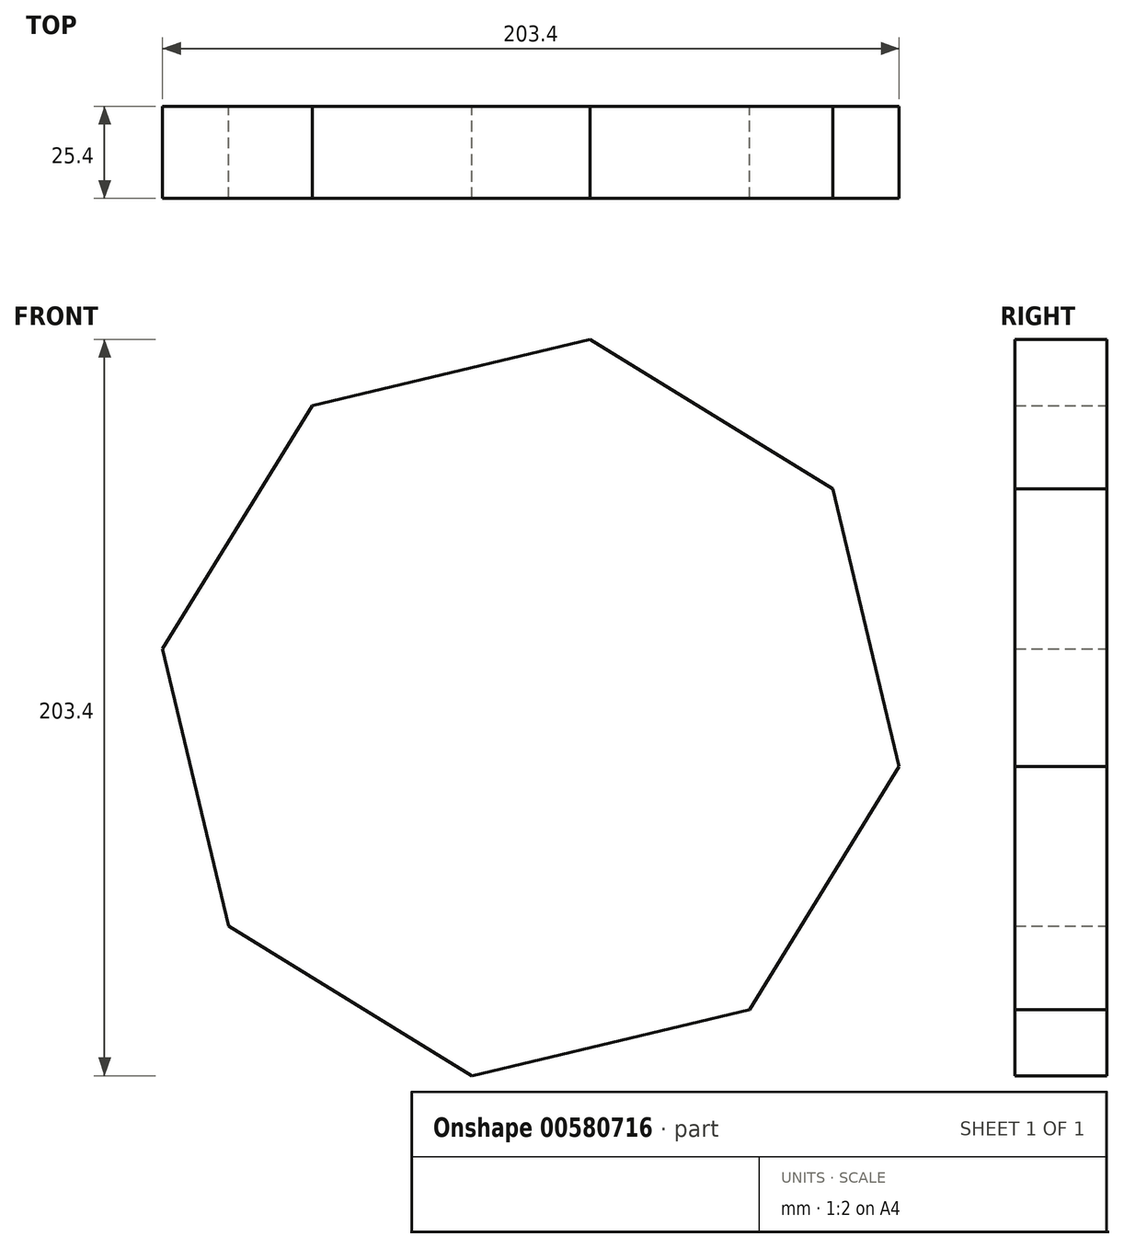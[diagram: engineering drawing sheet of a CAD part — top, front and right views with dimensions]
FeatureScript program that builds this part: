
annotation { "Feature Type Name" : "Feature", "Feature Type Description" : "" }
export const myFeature = defineFeature(function(context is Context, id is Id, definition is map)
    precondition{}
    {
        {
            var Q0;
            Q0=qCreatedBy(makeId("Front.planeOp"),FACE);
            var sketch = newSketch(context, id + "F0", { "sketchPlane" : qUnion([Q0])});
            skCircle(sketch, "E0.cCircle", {"center": v(0, 0) * mm, "radius": 91.98 * mm, "construction": true});
            skLineSegment(sketch, "E0.0", {"start": v(-98.3, 15.75) * mm, "end": v(-58.38, 80.65) * mm});
            skLineSegment(sketch, "E0.1", {"start": v(-58.38, 80.65) * mm, "end": v(15.75, 98.3) * mm, "construction": true});
            skLineSegment(sketch, "E0.2", {"start": v(15.75, 98.3) * mm, "end": v(80.65, 58.38) * mm});
            skLineSegment(sketch, "E0.3", {"start": v(80.65, 58.38) * mm, "end": v(98.3, -15.75) * mm});
            skLineSegment(sketch, "E0.4", {"start": v(98.3, -15.75) * mm, "end": v(58.38, -80.65) * mm});
            skLineSegment(sketch, "E0.5", {"start": v(58.38, -80.65) * mm, "end": v(-15.75, -98.3) * mm});
            skLineSegment(sketch, "E0.6", {"start": v(-15.75, -98.3) * mm, "end": v(-80.65, -58.38) * mm});
            skLineSegment(sketch, "E0.7", {"start": v(-80.65, -58.38) * mm, "end": v(-98.3, 15.75) * mm});
            skPoint(sketch, "E0.0.midPoint", {"position": v(-78.34, 48.2) * mm});
            skLineSegment(sketch, "E1.0", {"start": v(-101.7, 16.3) * mm, "end": v(-60.4, 83.43) * mm});
            skLineSegment(sketch, "E1.1", {"start": v(-83.43, -60.4) * mm, "end": v(-101.7, 16.3) * mm});
            skLineSegment(sketch, "E1.2", {"start": v(-60.4, 83.43) * mm, "end": v(16.3, 101.7) * mm});
            skLineSegment(sketch, "E1.3", {"start": v(-16.3, -101.7) * mm, "end": v(-83.43, -60.4) * mm});
            skLineSegment(sketch, "E1.4", {"start": v(16.3, 101.7) * mm, "end": v(83.43, 60.4) * mm});
            skLineSegment(sketch, "E1.5", {"start": v(83.43, 60.4) * mm, "end": v(101.7, -16.3) * mm});
            skLineSegment(sketch, "E1.6", {"start": v(101.7, -16.3) * mm, "end": v(60.4, -83.43) * mm});
            skLineSegment(sketch, "E1.7", {"start": v(60.4, -83.43) * mm, "end": v(-16.3, -101.7) * mm});
            skLineSegment(sketch, "E2", {"start": v(98.3, -15.75) * mm, "end": v(101.7, -16.3) * mm});
            skSolve(sketch);
        }
        {
            var Q0;
            Q0=makeQuery(id+"F0.imprint","IMPRINT",FACE,{"disambiguationData":[TD([[makeQuery(id+"F0.imprint","IMPRINT",EDGE,{"derivedFrom":sQuery(id+"F0.wireOp",EDGE,"E1.0")}),-1.0]])]});
            extrude(context, id + "F1", {"entities" : qUnion([Q0]), "depth" : 25.4 * mm, "offsetDistance" : 25.4 * mm});
        }
    });
